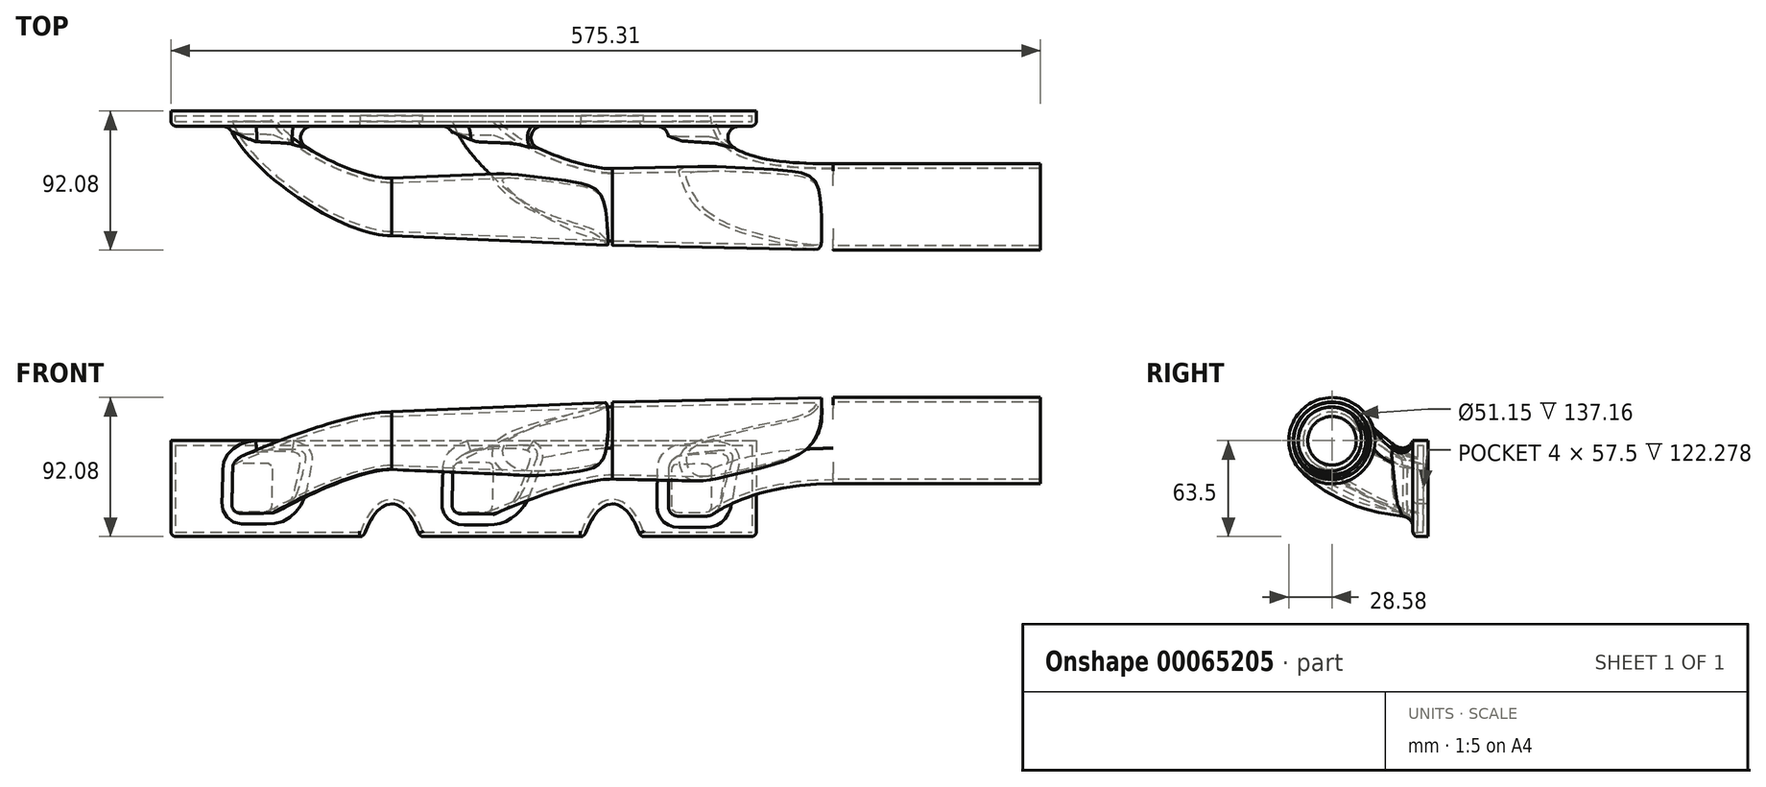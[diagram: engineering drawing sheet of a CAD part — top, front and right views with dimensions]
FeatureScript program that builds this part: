
annotation { "Feature Type Name" : "Feature", "Feature Type Description" : "" }
export const myFeature = defineFeature(function(context is Context, id is Id, definition is map)
    precondition{}
    {
        {
            var Q0;
            Q0=qCreatedBy(makeId("Front.planeOp"),FACE);
            var sketch = newSketch(context, id + "F0", { "sketchPlane" : qUnion([Q0])});
            skLineSegment(sketch, "E0.bottom", {"start": v(-146.05, 0) * mm, "end": v(241.3, 0) * mm});
            skLineSegment(sketch, "E0.top", {"start": v(-146.05, -63.5) * mm, "end": v(-18.63, -63.5) * mm});
            skLineSegment(sketch, "E0.left", {"start": v(-146.05, 0) * mm, "end": v(-146.05, -63.5) * mm});
            skLineSegment(sketch, "E0.right", {"start": v(241.3, 0) * mm, "end": v(241.3, -63.5) * mm});
            skEllipticalArc(sketch, "E1", {});
            skEllipticalArc(sketch, "E2.1.0.0", {});
            skLineSegment(sketch, "E3.trimOffspring", {"start": v(18.63, -63.5) * mm, "end": v(127.42, -63.5) * mm});
            skLineSegment(sketch, "E4.trimOffspring", {"start": v(164.68, -63.5) * mm, "end": v(241.3, -63.5) * mm});
            const initialGuessF0  = {"E1": [0, -0.09918, 0, 1, 0.05734, 0.023805, 5.3840067622967815, 0.8991785448828046], "E2.1.0.0": [0.14605, -0.09918, 0, 1, 0.05734, 0.023805, 5.3840067622967815, 0.8991785448828046]};
            skSetInitialGuess(sketch, initialGuessF0);
            skSolve(sketch);
        }
        {
            var Q0;
            Q0=qCreatedBy(makeId("Right.planeOp"),FACE);
            cPlane(context, id + "F1", {"entities" : qUnion([Q0]), "cplaneType" : CPlaneType.OFFSET, "offset" : 146.05 * mm, "width" : 152.4 * mm, "height" : 152.4 * mm});
        }
        {
            var Q0;
            Q0=qCreatedBy(id+"F1.planeOp",FACE);
            cPlane(context, id + "F2", {"entities" : qUnion([Q0]), "cplaneType" : CPlaneType.OFFSET, "offset" : 146.05 * mm, "width" : 152.4 * mm, "height" : 152.4 * mm});
        }
        {
            var Q0;
            Q0=qCreatedBy(makeId("Front.planeOp"),FACE);
            var sketch = newSketch(context, id + "F3", { "sketchPlane" : qUnion([Q0])});
            skLineSegment(sketch, "E5.rect.bottom", {"start": v(-103.5, -12.7) * mm, "end": v(-84.45, -12.7) * mm});
            skArc(sketch, "E6.filletArc", {"start": v(-78.1, -19.05) * mm, "mid": v(-79.96, -14.56) * mm, "end": v(-84.45, -12.7) * mm});
            skLineSegment(sketch, "E5.rect.right", {"start": v(-78.1, -19.05) * mm, "end": v(-78.1, -44.45) * mm});
            skArc(sketch, "E7.filletArc", {"start": v(-84.45, -50.8) * mm, "mid": v(-79.96, -48.94) * mm, "end": v(-78.1, -44.45) * mm});
            skLineSegment(sketch, "E5.rect.top", {"start": v(-103.5, -50.8) * mm, "end": v(-84.45, -50.8) * mm});
            skArc(sketch, "E8.filletArc", {"start": v(-109.86, -44.45) * mm, "mid": v(-108, -48.94) * mm, "end": v(-103.5, -50.8) * mm});
            skLineSegment(sketch, "E5.rect.left", {"start": v(-109.86, -19.05) * mm, "end": v(-109.86, -44.45) * mm});
            skArc(sketch, "E9.filletArc", {"start": v(-103.5, -12.7) * mm, "mid": v(-108, -14.56) * mm, "end": v(-109.86, -19.05) * mm});
            skLineSegment(sketch, "E10", {"start": v(-137.86, -31.75) * mm, "end": v(-109.86, -31.75) * mm, "construction": true});
            skPoint(sketch, "E10.startSnap0", {"position": v(-109.86, -31.75) * mm});
            skSolve(sketch);
        }
        {
            var Q0;
            Q0=qCreatedBy(makeId("Front.planeOp"),FACE);
            var sketch = newSketch(context, id + "F4", { "sketchPlane" : qUnion([Q0])});
            skLineSegment(sketch, "E11.rect.bottom", {"start": v(42.55, -12.7) * mm, "end": v(61.6, -12.7) * mm});
            skArc(sketch, "E12.filletArc", {"start": v(67.95, -19.05) * mm, "mid": v(66.09, -14.56) * mm, "end": v(61.6, -12.7) * mm});
            skLineSegment(sketch, "E11.rect.right", {"start": v(67.95, -19.05) * mm, "end": v(67.95, -44.45) * mm});
            skArc(sketch, "E13.filletArc", {"start": v(61.6, -50.8) * mm, "mid": v(66.09, -48.94) * mm, "end": v(67.95, -44.45) * mm});
            skLineSegment(sketch, "E11.rect.top", {"start": v(42.55, -50.8) * mm, "end": v(61.6, -50.8) * mm});
            skArc(sketch, "E14.filletArc", {"start": v(36.2, -44.45) * mm, "mid": v(38.05, -48.94) * mm, "end": v(42.55, -50.8) * mm});
            skLineSegment(sketch, "E11.rect.left", {"start": v(36.2, -19.05) * mm, "end": v(36.2, -44.45) * mm});
            skArc(sketch, "E15.filletArc", {"start": v(42.55, -12.7) * mm, "mid": v(38.05, -14.56) * mm, "end": v(36.2, -19.05) * mm});
            skLineSegment(sketch, "E16", {"start": v(36.2, -31.75) * mm, "end": v(-146.05, -31.75) * mm, "construction": true});
            skSolve(sketch);
        }
        {
            var Q0;
            Q0=qCreatedBy(makeId("Front.planeOp"),FACE);
            var sketch = newSketch(context, id + "F5", { "sketchPlane" : qUnion([Q0])});
            skLineSegment(sketch, "E17.rect.bottom", {"start": v(188.6, -12.7) * mm, "end": v(207.65, -12.7) * mm});
            skArc(sketch, "E18.filletArc", {"start": v(214, -19.05) * mm, "mid": v(212.14, -14.56) * mm, "end": v(207.65, -12.7) * mm});
            skLineSegment(sketch, "E17.rect.right", {"start": v(214, -19.05) * mm, "end": v(214, -44.45) * mm});
            skArc(sketch, "E19.filletArc", {"start": v(207.65, -50.8) * mm, "mid": v(212.14, -48.94) * mm, "end": v(214, -44.45) * mm});
            skLineSegment(sketch, "E17.rect.top", {"start": v(188.6, -50.8) * mm, "end": v(207.65, -50.8) * mm});
            skArc(sketch, "E20.filletArc", {"start": v(182.25, -44.45) * mm, "mid": v(184.1, -48.94) * mm, "end": v(188.6, -50.8) * mm});
            skLineSegment(sketch, "E17.rect.left", {"start": v(182.25, -19.05) * mm, "end": v(182.25, -44.45) * mm});
            skArc(sketch, "E21.filletArc", {"start": v(188.6, -12.7) * mm, "mid": v(184.1, -14.56) * mm, "end": v(182.25, -19.05) * mm});
            skLineSegment(sketch, "E22", {"start": v(182.25, -31.75) * mm, "end": v(-146.05, -31.75) * mm, "construction": true});
            skSolve(sketch);
        }
        {
            var Q0;
            Q0=qCreatedBy(makeId("Right.planeOp"),FACE);
            cPlane(context, id + "F6", {"entities" : qUnion([Q0]), "cplaneType" : CPlaneType.OFFSET, "offset" : 146.05 * mm, "width" : 152.4 * mm, "height" : 152.4 * mm});
        }
        {
            var Q0;
            Q0=qCreatedBy(makeId("Right.planeOp"),FACE);
            var sketch = newSketch(context, id + "F7", { "sketchPlane" : qUnion([Q0])});
            skCircle(sketch, "E23", {"center": v(-63.5, 0) * mm, "radius": 19.05 * mm});
            skSolve(sketch);
        }
        {
            var Q0;
            Q0=qCreatedBy(id+"F6.planeOp",FACE);
            var sketch = newSketch(context, id + "F8", { "sketchPlane" : qUnion([Q0])});
            skCircle(sketch, "E24", {"center": v(-63.5, 0) * mm, "radius": 25.4 * mm});
            skSolve(sketch);
        }
        {
            var Q0;
            Q0=qCreatedBy(id+"F2.planeOp",FACE);
            var sketch = newSketch(context, id + "F9", { "sketchPlane" : qUnion([Q0])});
            skCircle(sketch, "E25", {"center": v(-63.5, 0) * mm, "radius": 28.57 * mm});
            skSolve(sketch);
        }
        {
            var Q0;
            Q0=makeQuery(id+"F7.imprint","IMPRINT",FACE,{"disambiguationData":[TD([[makeQuery(id+"F7.imprint","IMPRINT",EDGE,{"derivedFrom":sQuery(id+"F7.wireOp",EDGE,"E23")}),1.0]])]});
            var Q1;
            Q1=makeQuery(id+"F8.imprint","IMPRINT",FACE,{"disambiguationData":[TD([[makeQuery(id+"F8.imprint","IMPRINT",EDGE,{"derivedFrom":sQuery(id+"F8.wireOp",EDGE,"E24")}),1.0]])]});
            loft(context, id + "F10", {"sheetProfilesArray" : [{ "sheetProfileEntities" : qUnion([Q0]) }, { "sheetProfileEntities" : qUnion([Q1]) }]});
        }
        {
            var Q1;
            Q1 = qSketchRegion(id + "F8", true);
            var Q2;
            Q2 = qSketchRegion(id + "F9", true);
            loft(context, id + "F11", {"operationType" : NewBodyOperationType.ADD, "sheetProfilesArray" : [{ "sheetProfileEntities" : qUnion([Q1]) }, { "sheetProfileEntities" : qUnion([Q2]) }]});
        }
        {
            var Q1;
            Q1 = qSketchRegion(id + "F7", true);
            var Q2;
            Q2 = qSketchRegion(id + "F3", true);
            loft(context, id + "F12", {"operationType" : NewBodyOperationType.ADD, "startCondition" : LoftEndDerivativeType.NORMAL_TO_PROFILE, "startMagnitude" : 1, "endCondition" : LoftEndDerivativeType.NORMAL_TO_PROFILE, "endMagnitude" : 1, "sheetProfilesArray" : [{ "sheetProfileEntities" : qUnion([Q1]) }, { "sheetProfileEntities" : qUnion([Q2]) }]});
        }
        {
            var Q1;
            Q1 = qSketchRegion(id + "F9", true);
            var Q2;
            Q2 = qSketchRegion(id + "F5", true);
            loft(context, id + "F13", {"operationType" : NewBodyOperationType.ADD, "startCondition" : LoftEndDerivativeType.NORMAL_TO_PROFILE, "startMagnitude" : 2, "endCondition" : LoftEndDerivativeType.NORMAL_TO_PROFILE, "endMagnitude" : 2, "sheetProfilesArray" : [{ "sheetProfileEntities" : qUnion([Q1]) }, { "sheetProfileEntities" : qUnion([Q2]) }]});
        }
        {
            var Q0;
            Q0=makeQuery(id+"F9.imprint","IMPRINT",FACE,{"disambiguationData":[TD([[makeQuery(id+"F9.imprint","IMPRINT",EDGE,{"derivedFrom":sQuery(id+"F9.wireOp",EDGE,"E25")}),1.0]])]});
            var sketch = newSketch(context, id + "F14", { "sketchPlane" : qUnion([Q0])});
            skCircle(sketch, "E26", {"center": v(-63.5, 0) * mm, "radius": 28.57 * mm});
            skSolve(sketch);
        }
        {
            var Q0;
            Q0 = qSketchRegion(id + "F14", true);
            extrude(context, id + "F15", {"entities" : qUnion([Q0]), "operationType" : NewBodyOperationType.ADD, "depth" : 137.16 * mm});
        }
        {
            var Q0;
            Q0 = qSketchRegion(id + "F0", true);
            extrude(context, id + "F16", {"entities" : qUnion([Q0]), "operationType" : NewBodyOperationType.ADD, "depth" : 10 * mm});
        }
        {
            var Q1;
            Q1 = qSketchRegion(id + "F8", true);
            var Q2;
            Q2 = qSketchRegion(id + "F4", true);
            loft(context, id + "F17", {"operationType" : NewBodyOperationType.ADD, "startCondition" : LoftEndDerivativeType.NORMAL_TO_PROFILE, "startMagnitude" : 1, "endCondition" : LoftEndDerivativeType.NORMAL_TO_PROFILE, "endMagnitude" : 1, "sheetProfilesArray" : [{ "sheetProfileEntities" : qUnion([Q1]) }, { "sheetProfileEntities" : qUnion([Q2]) }]});
        }
        {
            var Q0;
            Q0=makeQuery(id+"F15.opExtrude","CAP_FACE",FACE,{"disambiguationData":[OSD([sQuery(id+"F14.wireOp",EDGE,"E26")])],"isStart":false});
            var Q1;
            Q1=makeQuery(id+"F15.opExtrude","CAP_FACE",FACE,{"disambiguationData":[OSD([sQuery(id+"F14.wireOp",EDGE,"E26")])],"isStart":false});
            shell(context, id + "F18", {"entities" : qUnion([Q0, Q1]), "thickness" : 3 * mm});
        }
        {
            var Q0;
            Q0=makeQuery(id+"F16.boolean.opBoolean","INTERSECT",EDGE,{"derivedFrom":[makeQuery(id+"F12.opLoft","SWEPT_FACE",FACE,{"disambiguationData":[OSD([sQuery(id+"F3.wireOp",EDGE,"E5.rect.bottom"),sQuery(id+"F3.wireOp",EDGE,"E6.filletArc"),sQuery(id+"F3.wireOp",EDGE,"E5.rect.right"),sQuery(id+"F3.wireOp",EDGE,"E7.filletArc"),sQuery(id+"F3.wireOp",EDGE,"E9.filletArc"),sQuery(id+"F7.wireOp",EDGE,"E23")])]}),makeQuery(id+"F16.opExtrude","CAP_FACE",FACE,{"disambiguationData":[OSD([sQuery(id+"F0.wireOp",EDGE,"E0.bottom"),sQuery(id+"F0.wireOp",EDGE,"E0.top"),sQuery(id+"F0.wireOp",EDGE,"E0.left"),sQuery(id+"F0.wireOp",EDGE,"E0.right"),sQuery(id+"F0.wireOp",EDGE,"E1"),sQuery(id+"F0.wireOp",EDGE,"E2.1.0.0"),sQuery(id+"F0.wireOp",EDGE,"E3.trimOffspring"),sQuery(id+"F0.wireOp",EDGE,"E4.trimOffspring")])],"isStart":false})]});
            fillet(context, id + "F19", {"entities" : qUnion([Q0]), "radius" : 7.5 * mm, "tangentPropagation" : true, "allowEdgeOverflow" : false});
        }
        {
            var Q0;
            Q0=makeQuery(id+"F17.boolean.opBoolean","INTERSECT",EDGE,{"derivedFrom":[makeQuery(id+"F16.opExtrude","CAP_FACE",FACE,{"disambiguationData":[OSD([sQuery(id+"F0.wireOp",EDGE,"E0.bottom"),sQuery(id+"F0.wireOp",EDGE,"E0.top"),sQuery(id+"F0.wireOp",EDGE,"E0.left"),sQuery(id+"F0.wireOp",EDGE,"E0.right"),sQuery(id+"F0.wireOp",EDGE,"E1"),sQuery(id+"F0.wireOp",EDGE,"E2.1.0.0"),sQuery(id+"F0.wireOp",EDGE,"E3.trimOffspring"),sQuery(id+"F0.wireOp",EDGE,"E4.trimOffspring")])],"isStart":false}),makeQuery(id+"F17.opLoft","SWEPT_FACE",FACE,{"disambiguationData":[OSD([sQuery(id+"F4.wireOp",EDGE,"E11.rect.bottom"),sQuery(id+"F4.wireOp",EDGE,"E12.filletArc"),sQuery(id+"F4.wireOp",EDGE,"E11.rect.right"),sQuery(id+"F4.wireOp",EDGE,"E13.filletArc"),sQuery(id+"F4.wireOp",EDGE,"E15.filletArc"),sQuery(id+"F8.wireOp",EDGE,"E24")])]})]});
            fillet(context, id + "F20", {"entities" : qUnion([Q0]), "radius" : 7.5 * mm, "tangentPropagation" : true, "allowEdgeOverflow" : false});
        }
        {
            var Q0;
            Q0=makeQuery(id+"F16.boolean.opBoolean","INTERSECT",EDGE,{"derivedFrom":[makeQuery(id+"F13.opLoft","SWEPT_FACE",FACE,{"disambiguationData":[OSD([sQuery(id+"F5.wireOp",EDGE,"E17.rect.bottom"),sQuery(id+"F5.wireOp",EDGE,"E18.filletArc"),sQuery(id+"F5.wireOp",EDGE,"E17.rect.right"),sQuery(id+"F5.wireOp",EDGE,"E19.filletArc"),sQuery(id+"F5.wireOp",EDGE,"E21.filletArc"),sQuery(id+"F9.wireOp",EDGE,"E25")])]}),makeQuery(id+"F16.opExtrude","CAP_FACE",FACE,{"disambiguationData":[OSD([sQuery(id+"F0.wireOp",EDGE,"E0.bottom"),sQuery(id+"F0.wireOp",EDGE,"E0.top"),sQuery(id+"F0.wireOp",EDGE,"E0.left"),sQuery(id+"F0.wireOp",EDGE,"E0.right"),sQuery(id+"F0.wireOp",EDGE,"E1"),sQuery(id+"F0.wireOp",EDGE,"E2.1.0.0"),sQuery(id+"F0.wireOp",EDGE,"E3.trimOffspring"),sQuery(id+"F0.wireOp",EDGE,"E4.trimOffspring")])],"isStart":false})]});
            fillet(context, id + "F21", {"entities" : qUnion([Q0]), "radius" : 7.5 * mm, "tangentPropagation" : true, "allowEdgeOverflow" : false});
        }
        {
            var Q0;
            Q0=makeQuery(id+"F16.opExtrude","CAP_EDGE",EDGE,{"disambiguationData":[OSD([sQuery(id+"F0.wireOp",EDGE,"E0.top")])],"isStart":false});
            fillet(context, id + "F22", {"entities" : qUnion([Q0]), "radius" : 3.5 * mm, "tangentPropagation" : true, "allowEdgeOverflow" : false});
        }
        {
            var Q0;
            Q0=makeQuery(id+"F16.opExtrude","CAP_EDGE",EDGE,{"disambiguationData":[OSD([sQuery(id+"F0.wireOp",EDGE,"E0.left")])],"isStart":false});
            fillet(context, id + "F23", {"entities" : qUnion([Q0]), "radius" : 3.5 * mm, "tangentPropagation" : true, "allowEdgeOverflow" : false});
        }
        {
            var Q0;
            Q0=makeQuery(id+"F16.opExtrude","CAP_EDGE",EDGE,{"disambiguationData":[OSD([sQuery(id+"F0.wireOp",EDGE,"E1")])],"isStart":false});
            fillet(context, id + "F24", {"entities" : qUnion([Q0]), "radius" : 3.5 * mm, "tangentPropagation" : true, "allowEdgeOverflow" : false});
        }
        {
            var Q0;
            Q0=makeQuery(id+"F16.opExtrude","CAP_EDGE",EDGE,{"disambiguationData":[OSD([sQuery(id+"F0.wireOp",EDGE,"E3.trimOffspring")])],"isStart":false});
            fillet(context, id + "F25", {"entities" : qUnion([Q0]), "radius" : 3.5 * mm, "tangentPropagation" : true, "allowEdgeOverflow" : false});
        }
        {
            var Q0;
            Q0=makeQuery(id+"F16.opExtrude","CAP_EDGE",EDGE,{"disambiguationData":[OSD([sQuery(id+"F0.wireOp",EDGE,"E2.1.0.0")])],"isStart":false});
            fillet(context, id + "F26", {"entities" : qUnion([Q0]), "radius" : 3.5 * mm, "tangentPropagation" : true, "allowEdgeOverflow" : false});
        }
        {
            var Q0;
            Q0=makeQuery(id+"F16.opExtrude","CAP_EDGE",EDGE,{"disambiguationData":[OSD([sQuery(id+"F0.wireOp",EDGE,"E4.trimOffspring")])],"isStart":false});
            fillet(context, id + "F27", {"entities" : qUnion([Q0]), "radius" : 3.5 * mm, "tangentPropagation" : true, "allowEdgeOverflow" : false});
        }
        {
            var Q0;
            Q0=makeQuery(id+"F16.opExtrude","CAP_EDGE",EDGE,{"disambiguationData":[OSD([sQuery(id+"F0.wireOp",EDGE,"E0.right")])],"isStart":false});
            fillet(context, id + "F28", {"entities" : qUnion([Q0]), "radius" : 3.5 * mm, "tangentPropagation" : true, "allowEdgeOverflow" : false});
        }
    });
